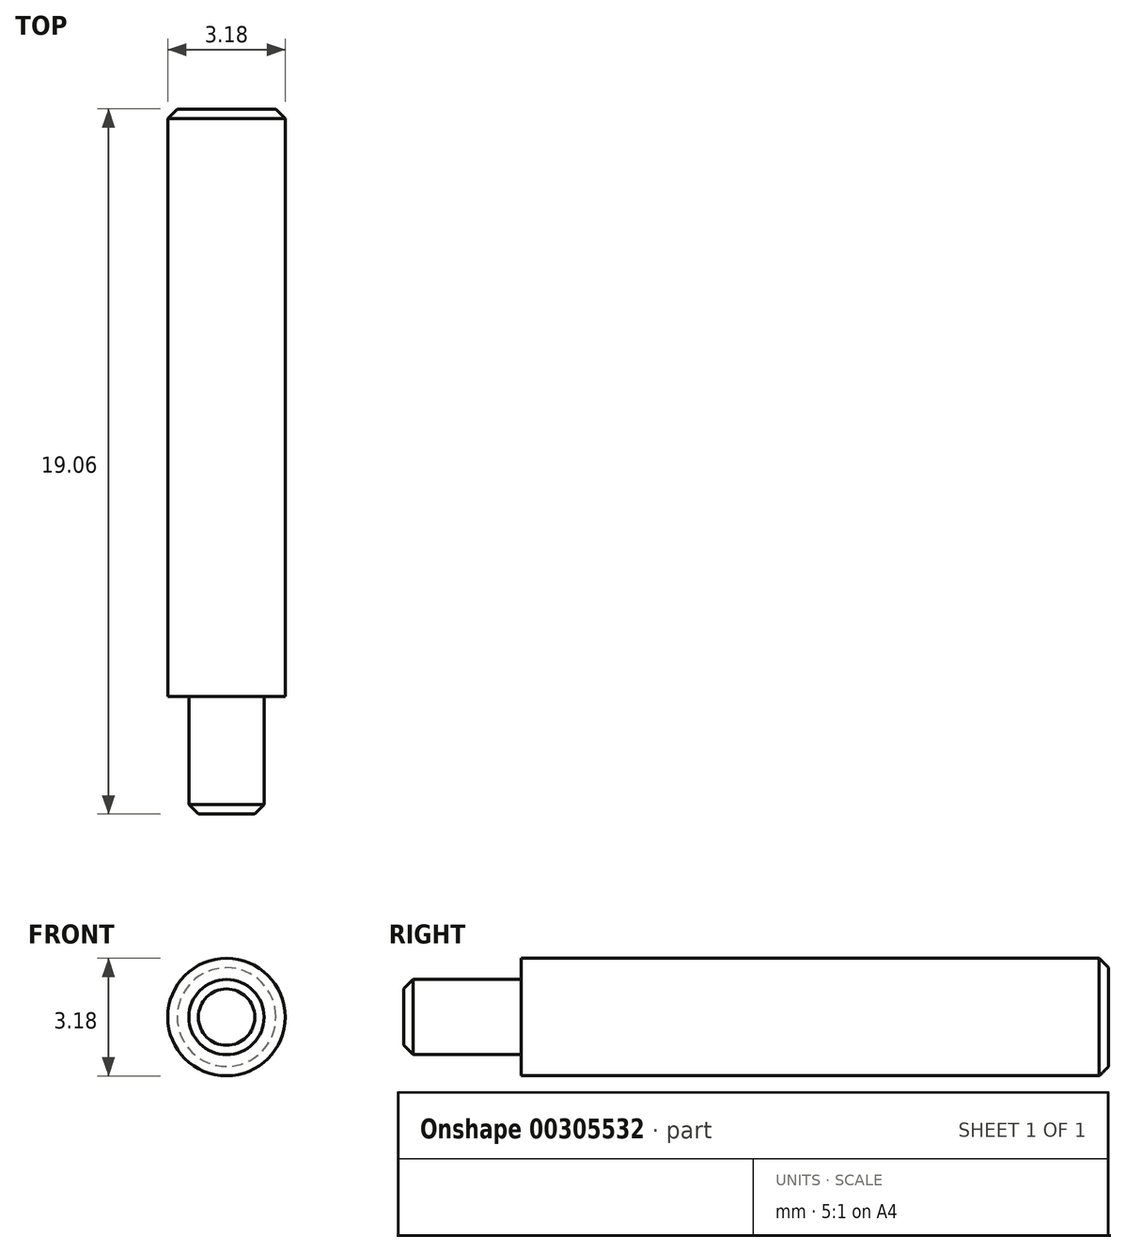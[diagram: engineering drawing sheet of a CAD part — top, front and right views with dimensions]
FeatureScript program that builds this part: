
annotation { "Feature Type Name" : "Feature", "Feature Type Description" : "" }
export const myFeature = defineFeature(function(context is Context, id is Id, definition is map)
    precondition{}
    {
        {
            var Q0;
            Q0=qCreatedBy(makeId("Front.planeOp"),FACE);
            var sketch = newSketch(context, id + "F0", { "sketchPlane" : qUnion([Q0])});
            skCircle(sketch, "E0", {"center": v(0, 0) * mm, "radius": 1.59 * mm});
            skCircle(sketch, "E1", {"center": v(0, 0) * mm, "radius": 1.02 * mm});
            skSolve(sketch);
        }
        {
            var Q0;
            Q0 = qSketchRegion(id + "F0", true);
            extrude(context, id + "F1", {"entities" : qUnion([Q0]), "oppositeDirection" : true, "depth" : 15.88 * mm});
        }
        {
            var Q0;
            Q0=makeQuery(id+"F0.imprint","IMPRINT",FACE,{"disambiguationData":[TD([[makeQuery(id+"F0.imprint","IMPRINT",EDGE,{"derivedFrom":sQuery(id+"F0.wireOp",EDGE,"E1")}),1.0]])]});
            extrude(context, id + "F2", {"entities" : qUnion([Q0]), "operationType" : NewBodyOperationType.ADD, "depth" : 3.17 * mm, "hasSecondDirection" : true, "secondDirectionOppositeDirection" : true, "secondDirectionDepth" : 15.88 * mm});
        }
        {
            var Q0;
            Q0=makeQuery(id+"F1.opExtrude","CAP_EDGE",EDGE,{"disambiguationData":[OSD([sQuery(id+"F0.wireOp",EDGE,"E0")])],"isStart":false});
            var Q1;
            Q1=makeQuery(id+"F2.opExtrude","CAP_EDGE",EDGE,{"disambiguationData":[OSD([sQuery(id+"F0.wireOp",EDGE,"E1")])],"isStart":false});
            chamfer(context, id + "F3", {"entities" : qUnion([Q0, Q1]), "width" : 0.25 * mm, "tangentPropagation" : true});
        }
    });
